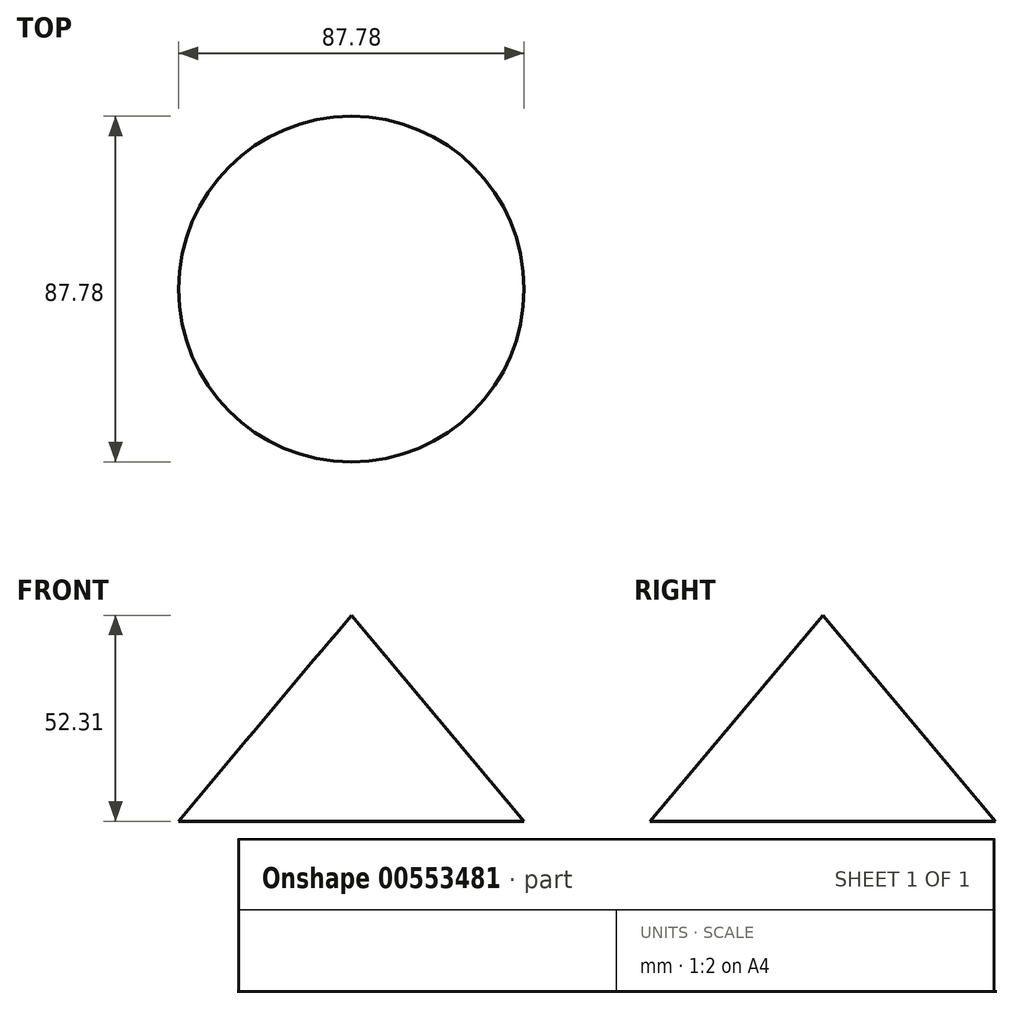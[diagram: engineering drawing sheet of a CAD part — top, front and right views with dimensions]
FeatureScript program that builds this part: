
annotation { "Feature Type Name" : "Feature", "Feature Type Description" : "" }
export const myFeature = defineFeature(function(context is Context, id is Id, definition is map)
    precondition{}
    {
        {
            var Q0;
            Q0=qCreatedBy(makeId("Front.planeOp"),FACE);
            var sketch = newSketch(context, id + "F0", { "sketchPlane" : qUnion([Q0])});
            skLineSegment(sketch, "E0", {"start": v(0, 0) * mm, "end": v(43.9, 0) * mm});
            skLineSegment(sketch, "E1", {"start": v(43.9, 0) * mm, "end": v(0, 52.31) * mm});
            skLineSegment(sketch, "E2", {"start": v(0, 52.31) * mm, "end": v(0, 0) * mm});
            skSolve(sketch);
        }
        {
            var Q0;
            Q0=makeQuery(id+"F0.imprint","IMPRINT",FACE,{"disambiguationData":[TD([[makeQuery(id+"F0.imprint","IMPRINT",EDGE,{"derivedFrom":sQuery(id+"F0.wireOp",EDGE,"E0")}),1.0]])]});
            var Q1;
            Q1=sQuery(id+"F0.wireOp",EDGE,"E2");
            revolve(context, id + "F1", {"entities" : qUnion([Q0]), "axis" : qUnion([Q1]), "revolveType" : RevolveType.FULL});
        }
    });
